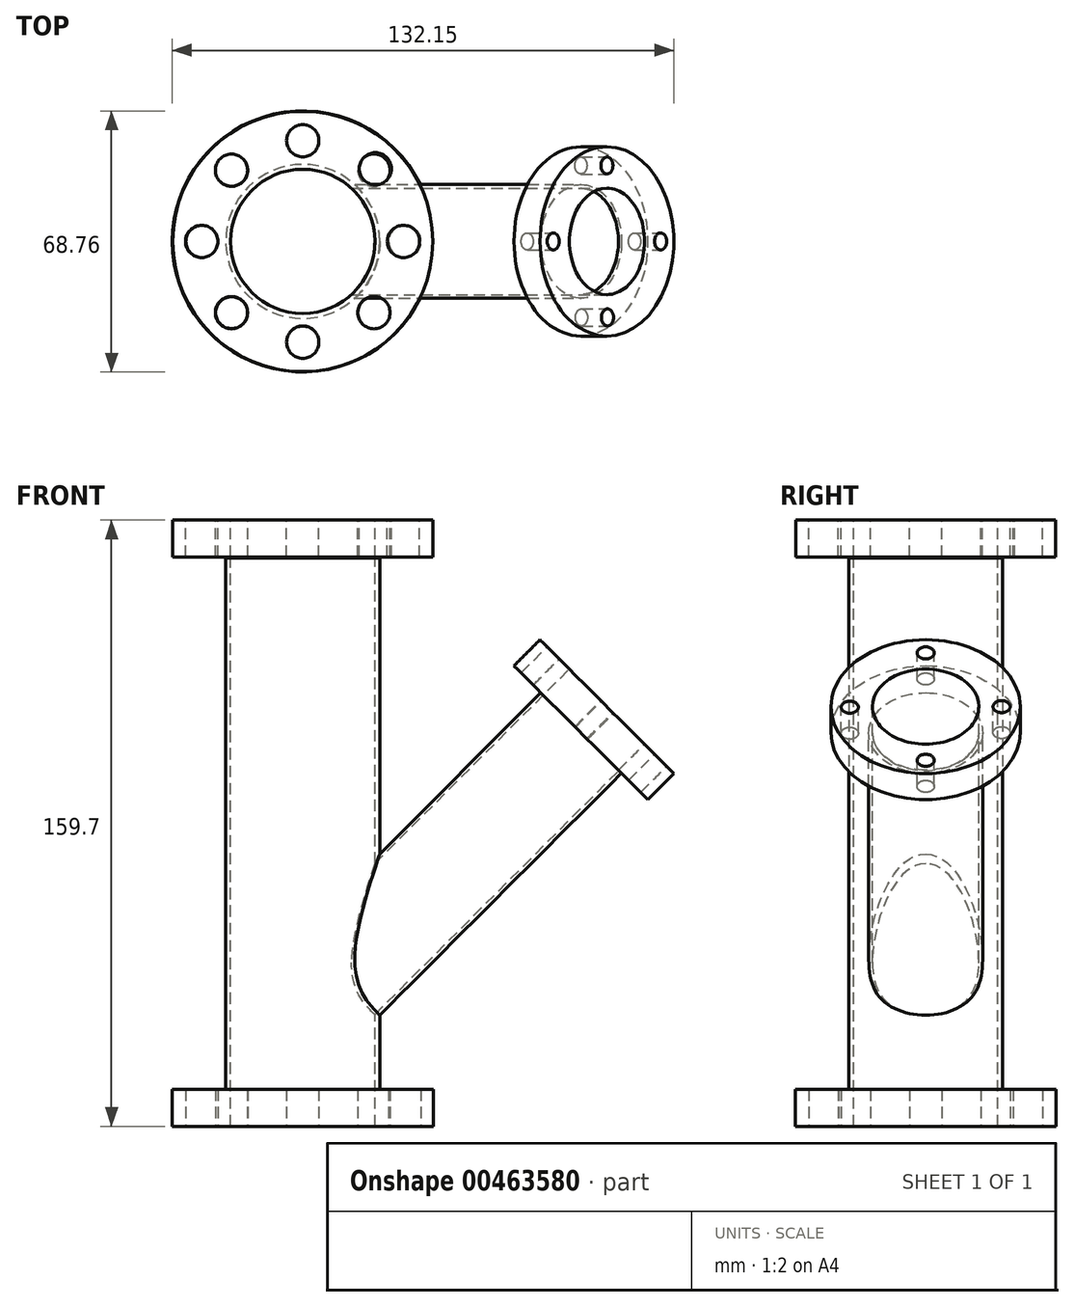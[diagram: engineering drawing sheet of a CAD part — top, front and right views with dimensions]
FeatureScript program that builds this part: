
annotation { "Feature Type Name" : "Feature", "Feature Type Description" : "" }
export const myFeature = defineFeature(function(context is Context, id is Id, definition is map)
    precondition{}
    {
        {
            var Q0;
            Q0=qCreatedBy(makeId("Top.planeOp"),FACE);
            var sketch = newSketch(context, id + "F0", { "sketchPlane" : qUnion([Q0])});
            skCircle(sketch, "E0", {"center": v(0, 0) * mm, "radius": 20.3 * mm});
            skSolve(sketch);
        }
        {
            var Q0;
            Q0 = qSketchRegion(id + "F0", true);
            extrude(context, id + "F1", {"entities" : qUnion([Q0]), "depth" : 140 * mm});
        }
        {
            var Q0;
            Q0=makeQuery(id+"F1.opExtrude","CAP_FACE",FACE,{"disambiguationData":[OSD([sQuery(id+"F0.wireOp",EDGE,"E0")])],"isStart":false});
            var sketch = newSketch(context, id + "F2", { "sketchPlane" : qUnion([Q0])});
            skCircle(sketch, "E1", {"center": v(0, 0) * mm, "radius": 19 * mm});
            skSolve(sketch);
        }
        {
            var Q0;
            Q0 = qSketchRegion(id + "F2", true);
            extrude(context, id + "F3", {"entities" : qUnion([Q0]), "operationType" : NewBodyOperationType.REMOVE, "oppositeDirection" : true, "depth" : 157 * mm});
        }
        {
            var Q0;
            Q0=qCreatedBy(makeId("Top.planeOp"),FACE);
            cPlane(context, id + "F4", {"entities" : qUnion([Q0]), "cplaneType" : CPlaneType.OFFSET, "offset" : 150 * mm, "width" : 150 * mm, "height" : 150 * mm});
        }
        {
            var Q0;
            Q0=qCreatedBy(id+"F4.planeOp",FACE);
            var sketch = newSketch(context, id + "F5", { "sketchPlane" : qUnion([Q0])});
            skCircle(sketch, "E2", {"center": v(0, 0) * mm, "radius": 34.27 * mm});
            skSolve(sketch);
        }
        {
            var Q0;
            Q0 = qSketchRegion(id + "F5", true);
            extrude(context, id + "F6", {"entities" : qUnion([Q0]), "oppositeDirection" : true, "depth" : 9.7 * mm});
        }
        {
            var Q0;
            Q0=makeQuery(id+"F6.opExtrude","CAP_FACE",FACE,{"disambiguationData":[OSD([sQuery(id+"F5.wireOp",EDGE,"E2")])],"isStart":true});
            var sketch = newSketch(context, id + "F7", { "sketchPlane" : qUnion([Q0])});
            skCircle(sketch, "E3", {"center": v(0, 0) * mm, "radius": 19 * mm});
            skSolve(sketch);
        }
        {
            var Q0;
            Q0 = qSketchRegion(id + "F7", true);
            extrude(context, id + "F8", {"entities" : qUnion([Q0]), "operationType" : NewBodyOperationType.REMOVE, "oppositeDirection" : true, "depth" : 204.2 * mm});
        }
        {
            var Q0;
            Q0=makeQuery(id+"F6.opExtrude","CAP_FACE",FACE,{"disambiguationData":[OSD([sQuery(id+"F5.wireOp",EDGE,"E2")])],"isStart":true});
            var sketch = newSketch(context, id + "F9", { "sketchPlane" : qUnion([Q0])});
            skLineSegment(sketch, "E4", {"start": v(0, 0) * mm, "end": v(0, 0) * mm});
            skLineSegment(sketch, "E5", {"start": v(26.54, 0) * mm, "end": v(55.72, 0) * mm});
            skPoint(sketch, "E6.start.orphan", {"position": v(-19, 0) * mm});
            skLineSegment(sketch, "E7", {"start": v(-19, 0) * mm, "end": v(-22.38, 0) * mm});
            skCircle(sketch, "E8", {"center": v(-26.63, 0) * mm, "radius": 4.25 * mm});
            skCircle(sketch, "E9", {"center": v(-18.76, 18.76) * mm, "radius": 4.25 * mm});
            skCircle(sketch, "E10", {"center": v(0, 26.54) * mm, "radius": 4.25 * mm});
            skCircle(sketch, "E11", {"center": v(19.14, 19.14) * mm, "radius": 4.25 * mm});
            skCircle(sketch, "E12", {"center": v(26.54, 0) * mm, "radius": 4.25 * mm});
            skCircle(sketch, "E13", {"center": v(18.76, -18.76) * mm, "radius": 4.25 * mm});
            skCircle(sketch, "E14", {"center": v(0, -26.54) * mm, "radius": 4.25 * mm});
            skCircle(sketch, "E15", {"center": v(-18.76, -18.76) * mm, "radius": 4.25 * mm});
            skPoint(sketch, "E16.trimOffspring.end.orphan", {"position": v(38.27, 38.27) * mm});
            skSolve(sketch);
        }
        {
            var Q0;
            Q0 = qSketchRegion(id + "F9", true);
            extrude(context, id + "F10", {"entities" : qUnion([Q0]), "operationType" : NewBodyOperationType.REMOVE, "oppositeDirection" : true, "depth" : 25 * mm});
        }
        {
            var Q0;
            Q0=qCreatedBy(makeId("Top.planeOp"),FACE);
            var sketch = newSketch(context, id + "F11", { "sketchPlane" : qUnion([Q0])});
            skCircle(sketch, "E17", {"center": v(0, 0) * mm, "radius": 34.38 * mm});
            skSolve(sketch);
        }
        {
            var Q0;
            Q0 = qSketchRegion(id + "F11", true);
            extrude(context, id + "F12", {"entities" : qUnion([Q0]), "operationType" : NewBodyOperationType.ADD, "oppositeDirection" : true, "depth" : 9.7 * mm});
        }
        {
            var Q0;
            Q0=makeQuery(id+"F12.opExtrude","CAP_FACE",FACE,{"disambiguationData":[OSD([sQuery(id+"F11.wireOp",EDGE,"E17")])],"isStart":false});
            var sketch = newSketch(context, id + "F13", { "sketchPlane" : qUnion([Q0])});
            skCircle(sketch, "E18", {"center": v(0, 0) * mm, "radius": 19 * mm});
            skSolve(sketch);
        }
        {
            var Q0;
            Q0 = qSketchRegion(id + "F13", true);
            extrude(context, id + "F14", {"entities" : qUnion([Q0]), "operationType" : NewBodyOperationType.REMOVE, "oppositeDirection" : true, "depth" : 168.4 * mm});
        }
        {
            var Q0;
            Q0=makeQuery(id+"F12.opExtrude","CAP_FACE",FACE,{"disambiguationData":[OSD([sQuery(id+"F11.wireOp",EDGE,"E17")])],"isStart":false});
            var sketch = newSketch(context, id + "F15", { "sketchPlane" : qUnion([Q0])});
            skLineSegment(sketch, "E19", {"start": v(-26.54, 0) * mm, "end": v(-26.69, 0) * mm});
            skPoint(sketch, "E20.orphan", {"position": v(-19, 0) * mm});
            skLineSegment(sketch, "E21", {"start": v(-26.69, 0) * mm, "end": v(-26.54, 0) * mm});
            skCircle(sketch, "E22", {"center": v(0, 26.54) * mm, "radius": 4.25 * mm});
            skCircle(sketch, "E23", {"center": v(18.77, 18.77) * mm, "radius": 4.25 * mm});
            skCircle(sketch, "E24", {"center": v(26.9, 0) * mm, "radius": 4.25 * mm});
            skCircle(sketch, "E25", {"center": v(18.77, -18.77) * mm, "radius": 4.25 * mm});
            skCircle(sketch, "E26", {"center": v(0, -26.54) * mm, "radius": 4.25 * mm});
            skCircle(sketch, "E27", {"center": v(-18.77, -18.77) * mm, "radius": 4.25 * mm});
            skCircle(sketch, "E28", {"center": v(-26.54, 0) * mm, "radius": 4.25 * mm});
            skCircle(sketch, "E29", {"center": v(-18.77, 18.77) * mm, "radius": 4.2 * mm});
            skPoint(sketch, "E30.orphan", {"position": v(53.82, 0) * mm});
            skPoint(sketch, "E31.center.orphan", {"position": v(0, 0) * mm});
            skSolve(sketch);
        }
        {
            var Q0;
            Q0 = qSketchRegion(id + "F15", true);
            extrude(context, id + "F16", {"entities" : qUnion([Q0]), "operationType" : NewBodyOperationType.REMOVE, "oppositeDirection" : true, "depth" : 25 * mm});
        }
        {
            var Q0;
            Q0=qCreatedBy(makeId("Front.planeOp"),FACE);
            var sketch = newSketch(context, id + "F17", { "sketchPlane" : qUnion([Q0])});
            skLineSegment(sketch, "E32", {"start": v(0, 0) * mm, "end": v(0, 40) * mm});
            skLineSegment(sketch, "E33", {"start": v(0, 40) * mm, "end": v(63.64, 103.64) * mm});
            skLineSegment(sketch, "E34", {"start": v(63.64, 103.64) * mm, "end": v(83.3, 83.97) * mm});
            skSolve(sketch);
        }
        {
            var Q0;
            Q0=qCreatedBy(makeId("Right.planeOp"),FACE);
            var Q1;
            Q1=sQuery(id+"F17.wireOp",EDGE,"E34");
            cPlane(context, id + "F18", {"entities" : qUnion([Q0, Q1]), "cplaneType" : CPlaneType.LINE_ANGLE, "offset" : 25 * mm, "angle" : 0 * degree, "width" : 150 * mm, "height" : 150 * mm});
        }
        {
            var Q0;
            Q0=qCreatedBy(id+"F18.planeOp",FACE);
            var sketch = newSketch(context, id + "F19", { "sketchPlane" : qUnion([Q0])});
            skCircle(sketch, "E35", {"center": v(0, 14.5) * mm, "radius": 15 * mm});
            skSolve(sketch);
        }
        {
            var Q0;
            Q0=makeQuery(id+"F19.imprint","IMPRINT",FACE,{"disambiguationData":[TD([[makeQuery(id+"F19.imprint","IMPRINT",EDGE,{"derivedFrom":sQuery(id+"F19.wireOp",EDGE,"E35")}),1.0]])]});
            var Q1;
            Q1=makeQuery(id+"F1.opExtrude","SWEPT_BODY",BODY,{"disambiguationData":[OSD([sQuery(id+"F0.wireOp",EDGE,"E0")])]});
            extrude(context, id + "F20", {"entities" : qUnion([Q0]), "operationType" : NewBodyOperationType.ADD, "endBound" : BoundingType.UP_TO_BODY, "endBoundEntityBody" : qUnion([Q1]), "depth" : 25 * mm});
        }
        {
            var Q0;
            Q0=makeQuery(id+"F20.opExtrude","CAP_FACE",FACE,{"disambiguationData":[OSD([sQuery(id+"F19.wireOp",EDGE,"E35")])],"isStart":true});
            var sketch = newSketch(context, id + "F21", { "sketchPlane" : qUnion([Q0])});
            skCircle(sketch, "E36", {"center": v(0, 14.5) * mm, "radius": 14 * mm});
            skLineSegment(sketch, "E37", {"start": v(14, 14.5) * mm, "end": v(15, 14.5) * mm});
            skSolve(sketch);
        }
        {
            var Q0;
            Q0 = qSketchRegion(id + "F21", true);
            extrude(context, id + "F22", {"entities" : qUnion([Q0]), "operationType" : NewBodyOperationType.REMOVE, "oppositeDirection" : true, "depth" : 104.3 * mm});
        }
        {
            var Q0;
            Q0=qCreatedBy(id+"F18.planeOp",FACE);
            var sketch = newSketch(context, id + "F23", { "sketchPlane" : qUnion([Q0])});
            skCircle(sketch, "E38", {"center": v(0, 16.3) * mm, "radius": 25 * mm});
            skSolve(sketch);
        }
        {
            var Q0;
            Q0=makeQuery(id+"F23.imprint","IMPRINT",FACE,{"disambiguationData":[TD([[makeQuery(id+"F23.imprint","IMPRINT",EDGE,{"derivedFrom":sQuery(id+"F23.wireOp",EDGE,"E38")}),1.0]])]});
            var sketch = newSketch(context, id + "F24", { "sketchPlane" : qUnion([Q0])});
            skCircle(sketch, "E39", {"center": v(0, 14.64) * mm, "radius": 24.92 * mm});
            skSolve(sketch);
        }
        {
            var Q0;
            Q0 = qSketchRegion(id + "F24", true);
            extrude(context, id + "F25", {"entities" : qUnion([Q0]), "operationType" : NewBodyOperationType.ADD, "oppositeDirection" : true, "depth" : 9.7 * mm});
        }
        {
            var Q0;
            Q0=makeQuery(id+"F25.opExtrude","CAP_FACE",FACE,{"disambiguationData":[OSD([sQuery(id+"F24.wireOp",EDGE,"E39")])],"isStart":false});
            var sketch = newSketch(context, id + "F26", { "sketchPlane" : qUnion([Q0])});
            skCircle(sketch, "E40", {"center": v(0, 14.64) * mm, "radius": 14 * mm});
            skSolve(sketch);
        }
        {
            var Q0;
            Q0 = qSketchRegion(id + "F26", true);
            extrude(context, id + "F27", {"entities" : qUnion([Q0]), "operationType" : NewBodyOperationType.REMOVE, "oppositeDirection" : true, "depth" : 120.7 * mm});
        }
        {
            var Q0;
            Q0=makeQuery(id+"F25.opExtrude","CAP_FACE",FACE,{"disambiguationData":[OSD([sQuery(id+"F24.wireOp",EDGE,"E39")])],"isStart":false});
            var sketch = newSketch(context, id + "F28", { "sketchPlane" : qUnion([Q0])});
            skLineSegment(sketch, "E41", {"start": v(0, 14.64) * mm, "end": v(0, 14.42) * mm});
            skLineSegment(sketch, "E42", {"start": v(22.26, 14.64) * mm, "end": v(24.92, 14.64) * mm});
            skLineSegment(sketch, "E43", {"start": v(24.92, 14.64) * mm, "end": v(22.26, 14.64) * mm});
            skLineSegment(sketch, "E44", {"start": v(0.35, 14.42) * mm, "end": v(0, 14.42) * mm});
            skCircle(sketch, "E45", {"center": v(-20, 14.42) * mm, "radius": 2.25 * mm});
            skCircle(sketch, "E46", {"center": v(0, 34.65) * mm, "radius": 2.25 * mm});
            skCircle(sketch, "E47", {"center": v(20, 14.64) * mm, "radius": 2.25 * mm});
            skCircle(sketch, "E48", {"center": v(0, -5.37) * mm, "radius": 2.25 * mm});
            skLineSegment(sketch, "E49.trimOffspring", {"start": v(0, 14.42) * mm, "end": v(0.35, 14.42) * mm});
            skLineSegment(sketch, "E50.trimOffspring", {"start": v(0, 14.42) * mm, "end": v(0, 14.64) * mm});
            skSolve(sketch);
        }
        {
            var Q0;
            Q0 = qSketchRegion(id + "F28", true);
            extrude(context, id + "F29", {"entities" : qUnion([Q0]), "operationType" : NewBodyOperationType.REMOVE, "oppositeDirection" : true, "depth" : 25 * mm});
        }
    });
